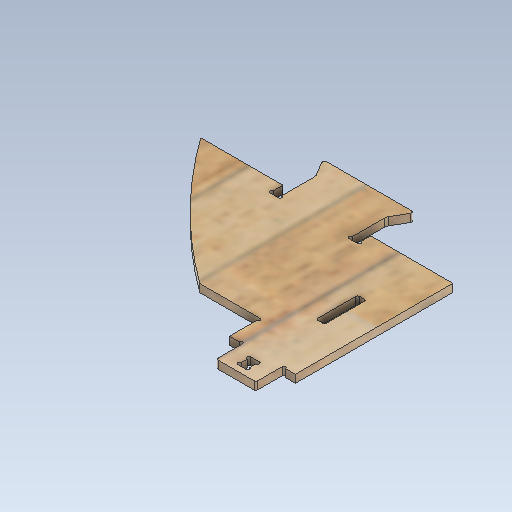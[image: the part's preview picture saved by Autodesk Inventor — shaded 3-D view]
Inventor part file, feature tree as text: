
AUTODESK INVENTOR PART (.ipt)
format: ipt  version: 2020 (Build 240168000, 168)  size: 265,728 bytes
history: native  units: mm
features: extrude x1, sketch x1
ambient origin geometry x8: Origin, YZ Plane, XZ Plane, XY Plane, X Axis, Y Axis, Z Axis, Center Point
bodies: Body1 (feature_tree)
feature tree (2):
  extrude  "Extrusion2"  Depth=30.0mm
  sketch  "Sketch1"  dims[d1=2.666667mm d2=30.0mm d3=20.0mm d4=2.666667mm d5=1.333333mm d6=7.333333mm d7=7.333333mm d8=20.666667mm d9=2.666667mm d10=45.833333mm d11=119.5mm d12=62.333333mm d17=2.666667mm d18=2.666667mm d19=7.333333mm d25=2.666667mm d26=65.0mm d27=425.0mm d39=44.0mm d53=2.666667mm d56=2.666667mm d57=4.5mm d58=5.5mm d59=6.5mm d63=1.333333mm d66=44.0mm d67=6.0mm d68=0.0mm d70=191.290163mm d71=62.333333mm d72=67.666667mm d73=9.371579mm d75=32.038246mm d76=60.0deg d79=5.0mm d80=70.645082mm]
